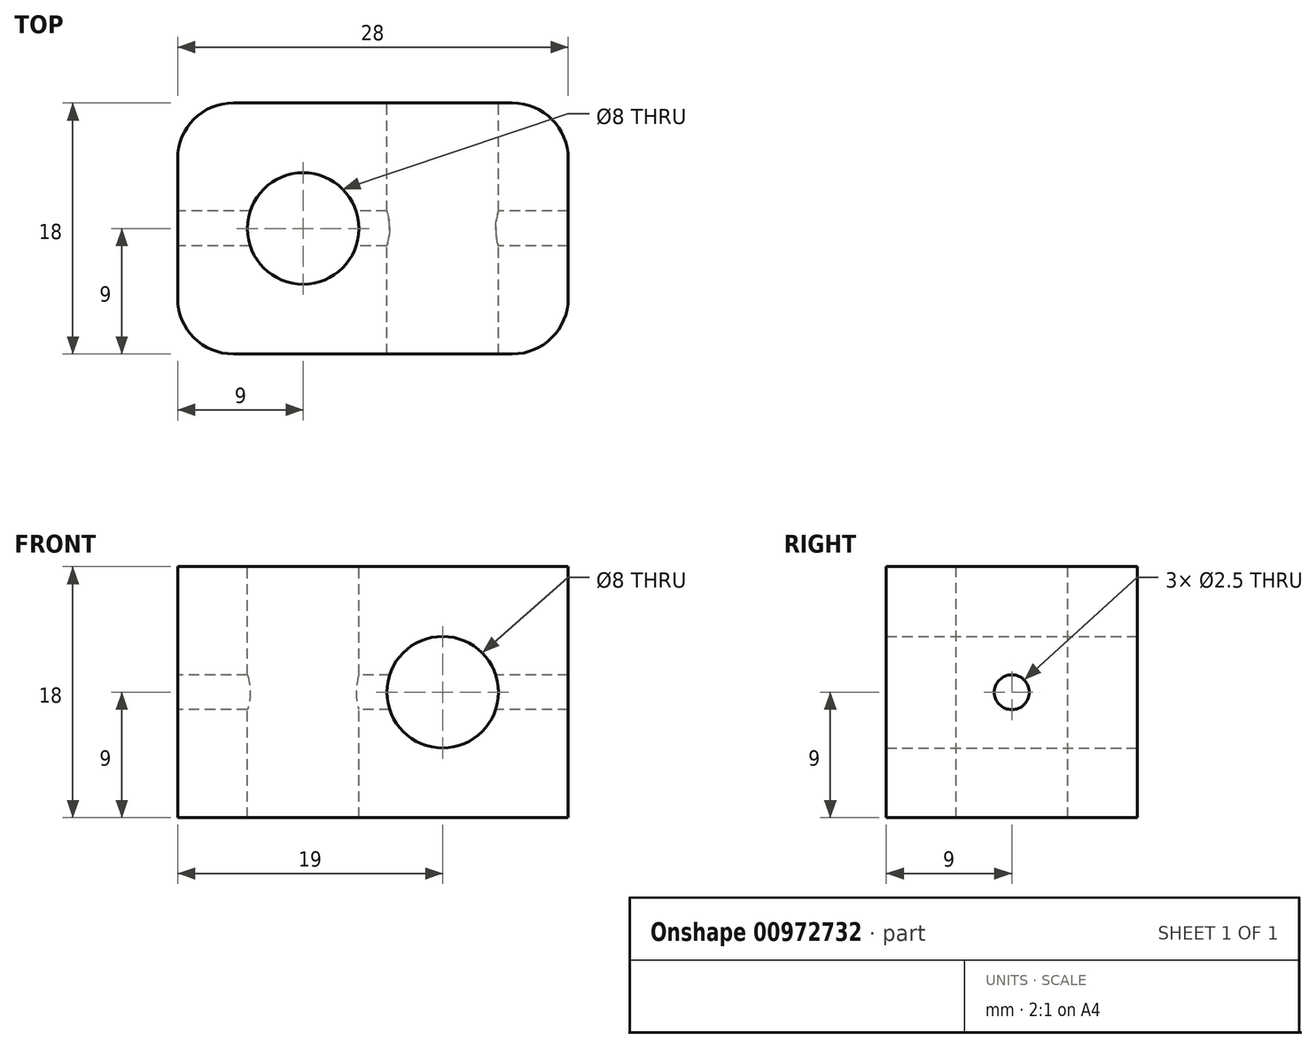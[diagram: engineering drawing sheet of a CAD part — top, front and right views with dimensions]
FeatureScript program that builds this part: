
annotation { "Feature Type Name" : "Feature", "Feature Type Description" : "" }
export const myFeature = defineFeature(function(context is Context, id is Id, definition is map)
    precondition{}
    {
        {
            var Q0;
            Q0=qCreatedBy(makeId("Top.planeOp"),FACE);
            var sketch = newSketch(context, id + "F0", { "sketchPlane" : qUnion([Q0])});
            skLineSegment(sketch, "E0.bottom", {"start": v(14, 9) * mm, "end": v(-14, 9) * mm});
            skLineSegment(sketch, "E0.top", {"start": v(14, -9) * mm, "end": v(-14, -9) * mm});
            skLineSegment(sketch, "E0.left", {"start": v(14, 9) * mm, "end": v(14, -9) * mm});
            skLineSegment(sketch, "E0.right", {"start": v(-14, 9) * mm, "end": v(-14, -9) * mm});
            skPoint(sketch, "E0.middle", {"position": v(0, 0) * mm});
            skSolve(sketch);
        }
        {
            var Q0;
            Q0=makeQuery(id+"F0.imprint","IMPRINT",FACE,{"disambiguationData":[TD([[makeQuery(id+"F0.imprint","IMPRINT",EDGE,{"derivedFrom":sQuery(id+"F0.wireOp",EDGE,"E0.bottom")}),1.0]])]});
            extrude(context, id + "F1", {"entities" : qUnion([Q0]), "depth" : 18 * mm, "offsetDistance" : 25 * mm});
        }
        {
            var Q0;
            Q0=makeQuery(id+"F1.opExtrude","CAP_FACE",FACE,{"disambiguationData":[OSD([sQuery(id+"F0.wireOp",EDGE,"E0.bottom"),sQuery(id+"F0.wireOp",EDGE,"E0.top"),sQuery(id+"F0.wireOp",EDGE,"E0.left"),sQuery(id+"F0.wireOp",EDGE,"E0.right")])],"isStart":false});
            var sketch = newSketch(context, id + "F2", { "sketchPlane" : qUnion([Q0])});
            skCircle(sketch, "E1", {"center": v(-5, 0) * mm, "radius": 4 * mm});
            skSolve(sketch);
        }
        {
            var Q0;
            Q0=makeQuery(id+"F1.opExtrude","SWEPT_FACE",FACE,{"disambiguationData":[OSD([sQuery(id+"F0.wireOp",EDGE,"E0.bottom")])]});
            var sketch = newSketch(context, id + "F3", { "sketchPlane" : qUnion([Q0])});
            skCircle(sketch, "E2", {"center": v(-5, 9) * mm, "radius": 4 * mm});
            skSolve(sketch);
        }
        {
            var Q0;
            Q0=makeQuery(id+"F2.imprint","IMPRINT",FACE,{"disambiguationData":[TD([[makeQuery(id+"F2.imprint","IMPRINT",EDGE,{"derivedFrom":sQuery(id+"F2.wireOp",EDGE,"E1")}),1.0]])]});
            extrude(context, id + "F4", {"entities" : qUnion([Q0]), "operationType" : NewBodyOperationType.REMOVE, "endBound" : BoundingType.THROUGH_ALL, "oppositeDirection" : true, "depth" : 25 * mm, "offsetDistance" : 25 * mm});
        }
        {
            var Q0;
            Q0=makeQuery(id+"F3.imprint","IMPRINT",FACE,{"disambiguationData":[TD([[makeQuery(id+"F3.imprint","IMPRINT",EDGE,{"derivedFrom":sQuery(id+"F3.wireOp",EDGE,"E2")}),1.0]])]});
            extrude(context, id + "F5", {"entities" : qUnion([Q0]), "operationType" : NewBodyOperationType.REMOVE, "endBound" : BoundingType.THROUGH_ALL, "oppositeDirection" : true, "depth" : 25 * mm, "offsetDistance" : 25 * mm});
        }
        {
            var Q0;
            Q0=makeQuery(id+"F1.opExtrude","SWEPT_FACE",FACE,{"disambiguationData":[OSD([sQuery(id+"F0.wireOp",EDGE,"E0.right")])]});
            var sketch = newSketch(context, id + "F6", { "sketchPlane" : qUnion([Q0])});
            skCircle(sketch, "E3", {"center": v(0, 9) * mm, "radius": 1.25 * mm});
            skSolve(sketch);
        }
        {
            var Q0;
            Q0=makeQuery(id+"F6.imprint","IMPRINT",FACE,{"disambiguationData":[TD([[makeQuery(id+"F6.imprint","IMPRINT",EDGE,{"derivedFrom":sQuery(id+"F6.wireOp",EDGE,"E3")}),1.0]])]});
            extrude(context, id + "F7", {"entities" : qUnion([Q0]), "operationType" : NewBodyOperationType.REMOVE, "endBound" : BoundingType.THROUGH_ALL, "oppositeDirection" : true, "depth" : 25 * mm, "offsetDistance" : 25 * mm});
        }
        {
            var Q0;
            Q0=makeQuery(id+"F1.opExtrude","SWEPT_EDGE",EDGE,{"disambiguationData":[OSD([sQuery(id+"F0.wireOp",EDGE,"E0.top"),sQuery(id+"F0.wireOp",EDGE,"E0.right")])]});
            var Q1;
            Q1=makeQuery(id+"F1.opExtrude","SWEPT_EDGE",EDGE,{"disambiguationData":[OSD([sQuery(id+"F0.wireOp",EDGE,"E0.bottom"),sQuery(id+"F0.wireOp",EDGE,"E0.right")])]});
            var Q2;
            Q2=makeQuery(id+"F1.opExtrude","SWEPT_EDGE",EDGE,{"disambiguationData":[OSD([sQuery(id+"F0.wireOp",EDGE,"E0.top"),sQuery(id+"F0.wireOp",EDGE,"E0.left")])]});
            var Q3;
            Q3=makeQuery(id+"F1.opExtrude","SWEPT_EDGE",EDGE,{"disambiguationData":[OSD([sQuery(id+"F0.wireOp",EDGE,"E0.bottom"),sQuery(id+"F0.wireOp",EDGE,"E0.left")])]});
            fillet(context, id + "F8", {"entities" : qUnion([Q0, Q1, Q2, Q3]), "radius" : 4 * mm, "tangentPropagation" : true, "allowEdgeOverflow" : false});
        }
    });
